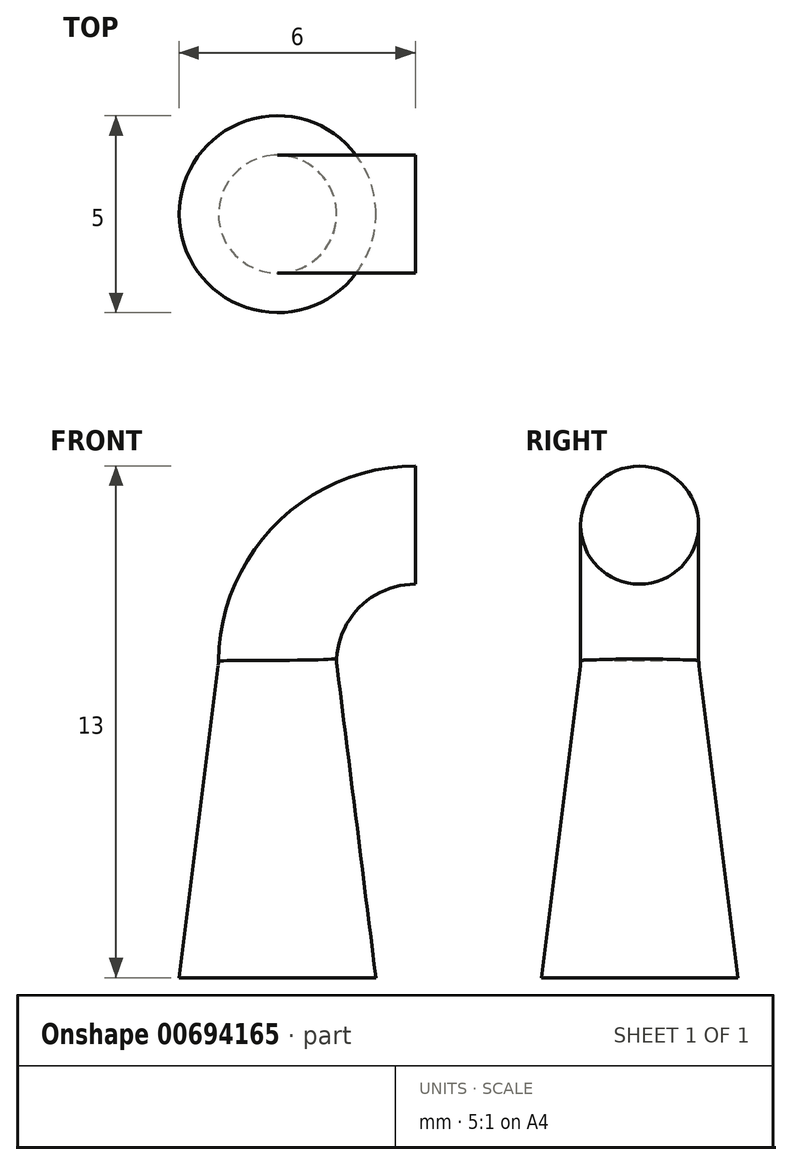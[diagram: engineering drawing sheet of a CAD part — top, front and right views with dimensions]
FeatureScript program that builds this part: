
annotation { "Feature Type Name" : "Feature", "Feature Type Description" : "" }
export const myFeature = defineFeature(function(context is Context, id is Id, definition is map)
    precondition{}
    {
        {
            var Q0;
            Q0=qCreatedBy(makeId("Top.planeOp"),FACE);
            var sketch = newSketch(context, id + "F0", { "sketchPlane" : qUnion([Q0])});
            skCircle(sketch, "E0", {"center": v(0, 0) * mm, "radius": 2.5 * mm});
            skSolve(sketch);
        }
        {
            var Q0;
            Q0=qCreatedBy(makeId("Top.planeOp"),FACE);
            cPlane(context, id + "F1", {"entities" : qUnion([Q0]), "cplaneType" : CPlaneType.OFFSET, "offset" : 8 * mm, "width" : 150 * mm, "height" : 150 * mm});
        }
        {
            var Q0;
            Q0=qCreatedBy(id+"F1.planeOp",FACE);
            var sketch = newSketch(context, id + "F2", { "sketchPlane" : qUnion([Q0])});
            skCircle(sketch, "E1", {"center": v(0, 0) * mm, "radius": 1.5 * mm});
            skSolve(sketch);
        }
        {
            var Q0;
            Q0=makeQuery(id+"F0.imprint","IMPRINT",FACE,{"disambiguationData":[TD([[makeQuery(id+"F0.imprint","IMPRINT",EDGE,{"derivedFrom":sQuery(id+"F0.wireOp",EDGE,"E0")}),1.0]])]});
            var Q1;
            Q1=makeQuery(id+"F2.imprint","IMPRINT",FACE,{"disambiguationData":[TD([[makeQuery(id+"F2.imprint","IMPRINT",EDGE,{"derivedFrom":sQuery(id+"F2.wireOp",EDGE,"E1")}),1.0]])]});
            loft(context, id + "F3", {"sheetProfilesArray" : [{ "sheetProfileEntities" : qUnion([Q0]) }, { "sheetProfileEntities" : qUnion([Q1]) }]});
        }
        {
            var Q0;
            Q0=qCreatedBy(makeId("Right.planeOp"),FACE);
            cPlane(context, id + "F4", {"entities" : qUnion([Q0]), "cplaneType" : CPlaneType.OFFSET, "offset" : 3.5 * mm, "width" : 150 * mm, "height" : 150 * mm});
        }
        {
            var Q0;
            Q0=qCreatedBy(id+"F4.planeOp",FACE);
            var sketch = newSketch(context, id + "F5", { "sketchPlane" : qUnion([Q0])});
            skLineSegment(sketch, "E2", {"start": v(0, 0) * mm, "end": v(0, 11.5) * mm, "construction": true});
            skCircle(sketch, "E3", {"center": v(0, 11.5) * mm, "radius": 1.5 * mm});
            skSolve(sketch);
        }
        {
            var Q0;
            Q0=qCreatedBy(makeId("Front.planeOp"),FACE);
            var sketch = newSketch(context, id + "F6", { "sketchPlane" : qUnion([Q0])});
            skArc(sketch, "E4", {"start": v(3.5, 10.75) * mm, "mid": v(1.56, 9.94) * mm, "end": v(0.75, 8) * mm});
            skSolve(sketch);
        }
        {
            var Q0;
            Q0=makeQuery(id+"F5.imprint","IMPRINT",FACE,{"disambiguationData":[TD([[makeQuery(id+"F5.imprint","IMPRINT",EDGE,{"derivedFrom":sQuery(id+"F5.wireOp",EDGE,"E3")}),1.0]])]});
            var Q1;
            Q1=sQuery(id+"F6.wireOp",EDGE,"E4");
            sweep(context, id + "F7", {"operationType" : NewBodyOperationType.ADD, "profiles" : qUnion([Q0]), "path" : qUnion([Q1])});
        }
        {
            var Q0;
            Q0=makeQuery(id+"F7.boolean.opBoolean","MERGE",EDGE,{"derivedFrom":[makeQuery(id+"F3.opLoft","MID_CAP_EDGE",EDGE,{"disambiguationData":[OSD([sQuery(id+"F0.wireOp",EDGE,"E0"),sQuery(id+"F2.wireOp",EDGE,"E1")])],"capPos":1.0}),makeQuery(id+"F7.opSweep","CAP_EDGE",EDGE,{"disambiguationData":[OSD([sQuery(id+"F5.wireOp",EDGE,"E3"),sQuery(id+"F6.wireOp",VERTEX,"E4.end")])],"isStart":false})]});
            fillet(context, id + "F8", {"entities" : qUnion([Q0]), "radius" : 1 * mm, "tangentPropagation" : true, "allowEdgeOverflow" : false});
        }
    });
